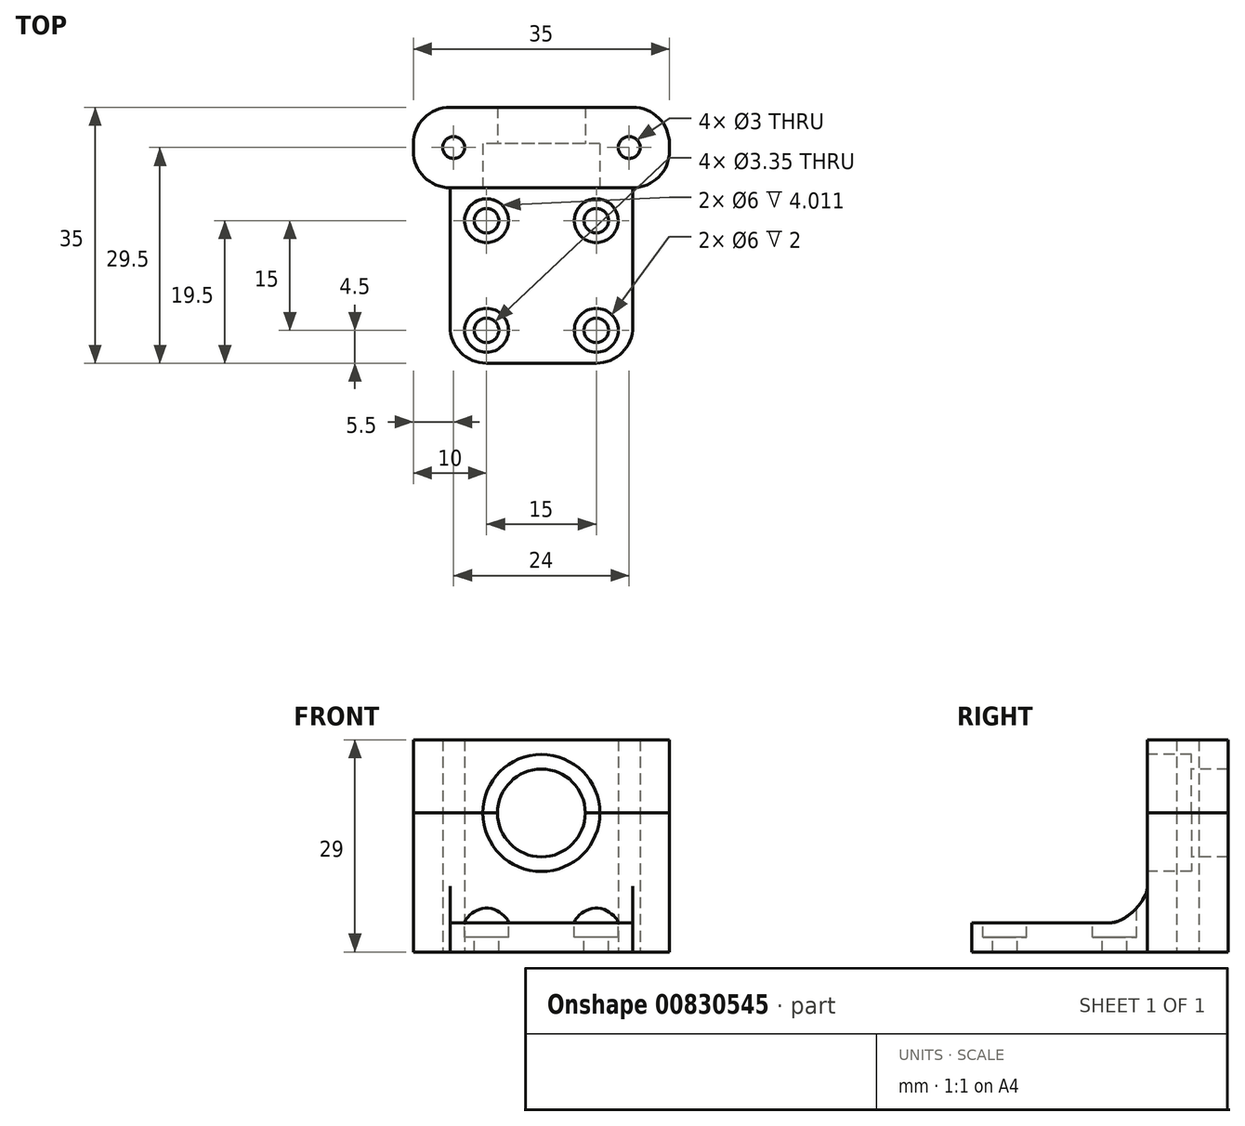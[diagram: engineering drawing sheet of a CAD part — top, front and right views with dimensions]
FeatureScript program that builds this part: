
annotation { "Feature Type Name" : "Feature", "Feature Type Description" : "" }
export const myFeature = defineFeature(function(context is Context, id is Id, definition is map)
    precondition{}
    {
        {
            var Q0;
            Q0=qCreatedBy(makeId("Right.planeOp"),FACE);
            var sketch = newSketch(context, id + "F0", { "sketchPlane" : qUnion([Q0])});
            skLineSegment(sketch, "E0", {"start": v(-12, -2) * mm, "end": v(23, -2) * mm});
            skLineSegment(sketch, "E1", {"start": v(23, -2) * mm, "end": v(23, 17) * mm});
            skLineSegment(sketch, "E2", {"start": v(23, 17) * mm, "end": v(12, 17) * mm});
            skLineSegment(sketch, "E3", {"start": v(12, 17) * mm, "end": v(12, 2) * mm});
            skLineSegment(sketch, "E4", {"start": v(12, 2) * mm, "end": v(-12, 2) * mm});
            skLineSegment(sketch, "E5", {"start": v(-12, 2) * mm, "end": v(-12, -2) * mm});
            skSolve(sketch);
        }
        {
            var Q0;
            Q0=qSketchRegion(id+"F0",true);
            extrude(context, id + "F1", {"entities" : qUnion([Q0]), "endBound" : BoundingType.SYMMETRIC, "depth" : 25 * mm, "offsetDistance" : 25 * mm});
        }
        {
            var Q0;
            Q0=makeQuery(id+"F1.opExtrude","SWEPT_FACE",FACE,{"disambiguationData":[OSD([sQuery(id+"F0.wireOp",EDGE,"E0")])]});
            var sketch = newSketch(context, id + "F2", { "sketchPlane" : qUnion([Q0])});
            skLineSegment(sketch, "E6.bottom", {"start": v(-17.5, -23) * mm, "end": v(17.5, -23) * mm});
            skLineSegment(sketch, "E6.top", {"start": v(-17.5, -12) * mm, "end": v(17.5, -12) * mm});
            skLineSegment(sketch, "E6.left", {"start": v(-17.5, -23) * mm, "end": v(-17.5, -12) * mm});
            skLineSegment(sketch, "E6.right", {"start": v(17.5, -23) * mm, "end": v(17.5, -12) * mm});
            skSolve(sketch);
        }
        {
            var Q0;
            Q0=qSketchRegion(id+"F2",true);
            var Q1;
            Q1=makeQuery(id+"F1.opExtrude","SWEPT_FACE",FACE,{"disambiguationData":[OSD([sQuery(id+"F0.wireOp",EDGE,"E2")])]});
            extrude(context, id + "F3", {"entities" : qUnion([Q0]), "operationType" : NewBodyOperationType.ADD, "endBound" : BoundingType.UP_TO_SURFACE, "oppositeDirection" : true, "depth" : 25 * mm, "endBoundEntityFace" : qUnion([Q1]), "offsetDistance" : 25 * mm});
        }
        {
            var Q0;
            Q0=makeQuery(id+"F1.opExtrude","SWEPT_FACE",FACE,{"disambiguationData":[OSD([sQuery(id+"F0.wireOp",EDGE,"E4")])]});
            var sketch = newSketch(context, id + "F4", { "sketchPlane" : qUnion([Q0])});
            skLineSegment(sketch, "E7.bottom", {"start": v(7.5, -7.5) * mm, "end": v(-7.5, -7.5) * mm, "construction": true});
            skLineSegment(sketch, "E7.top", {"start": v(7.5, 7.5) * mm, "end": v(-7.5, 7.5) * mm, "construction": true});
            skLineSegment(sketch, "E7.left", {"start": v(7.5, -7.5) * mm, "end": v(7.5, 7.5) * mm, "construction": true});
            skLineSegment(sketch, "E7.right", {"start": v(-7.5, -7.5) * mm, "end": v(-7.5, 7.5) * mm, "construction": true});
            skPoint(sketch, "E7.middle", {"position": v(0, 0) * mm});
            skCircle(sketch, "E8", {"center": v(7.5, 7.5) * mm, "radius": 3 * mm});
            skCircle(sketch, "E9", {"center": v(7.5, 7.5) * mm, "radius": 1.68 * mm});
            skCircle(sketch, "E10", {"center": v(7.5, -7.5) * mm, "radius": 3 * mm});
            skCircle(sketch, "E11", {"center": v(7.5, -7.5) * mm, "radius": 1.68 * mm});
            skCircle(sketch, "E12", {"center": v(-7.5, -7.5) * mm, "radius": 3 * mm});
            skCircle(sketch, "E13", {"center": v(-7.5, -7.5) * mm, "radius": 1.68 * mm});
            skCircle(sketch, "E14", {"center": v(-7.5, 7.5) * mm, "radius": 3 * mm});
            skCircle(sketch, "E15", {"center": v(-7.5, 7.5) * mm, "radius": 1.68 * mm});
            skSolve(sketch);
        }
        {
            var Q0;
            Q0=makeQuery(id+"F4.imprint","IMPRINT",FACE,{"disambiguationData":[TD([[makeQuery(id+"F4.imprint","IMPRINT",EDGE,{"derivedFrom":sQuery(id+"F4.wireOp",EDGE,"E9")}),1.0]])]});
            var Q1;
            Q1=makeQuery(id+"F4.imprint","IMPRINT",FACE,{"disambiguationData":[TD([[makeQuery(id+"F4.imprint","IMPRINT",EDGE,{"derivedFrom":sQuery(id+"F4.wireOp",EDGE,"E11")}),1.0]])]});
            var Q2;
            Q2=makeQuery(id+"F4.imprint","IMPRINT",FACE,{"disambiguationData":[TD([[makeQuery(id+"F4.imprint","IMPRINT",EDGE,{"derivedFrom":sQuery(id+"F4.wireOp",EDGE,"E13")}),1.0]])]});
            var Q3;
            Q3=makeQuery(id+"F4.imprint","IMPRINT",FACE,{"disambiguationData":[TD([[makeQuery(id+"F4.imprint","IMPRINT",EDGE,{"derivedFrom":sQuery(id+"F4.wireOp",EDGE,"E15")}),1.0]])]});
            extrude(context, id + "F5", {"entities" : qUnion([Q0, Q1, Q2, Q3]), "operationType" : NewBodyOperationType.REMOVE, "endBound" : BoundingType.THROUGH_ALL, "oppositeDirection" : true, "depth" : 25 * mm, "offsetDistance" : 25 * mm});
        }
        {
            var Q0;
            Q0=makeQuery(id+"F4.imprint","IMPRINT",FACE,{"disambiguationData":[TD([[makeQuery(id+"F4.imprint","IMPRINT",EDGE,{"derivedFrom":sQuery(id+"F4.wireOp",EDGE,"E14")}),1.0]])]});
            var Q1;
            Q1=makeQuery(id+"F4.imprint","IMPRINT",FACE,{"disambiguationData":[TD([[makeQuery(id+"F4.imprint","IMPRINT",EDGE,{"derivedFrom":sQuery(id+"F4.wireOp",EDGE,"E8")}),1.0]])]});
            var Q2;
            Q2=makeQuery(id+"F4.imprint","IMPRINT",FACE,{"disambiguationData":[TD([[makeQuery(id+"F4.imprint","IMPRINT",EDGE,{"derivedFrom":sQuery(id+"F4.wireOp",EDGE,"E10")}),1.0]])]});
            var Q3;
            Q3=makeQuery(id+"F4.imprint","IMPRINT",FACE,{"disambiguationData":[TD([[makeQuery(id+"F4.imprint","IMPRINT",EDGE,{"derivedFrom":sQuery(id+"F4.wireOp",EDGE,"E12")}),1.0]])]});
            extrude(context, id + "F6", {"entities" : qUnion([Q0, Q1, Q2, Q3]), "operationType" : NewBodyOperationType.REMOVE, "oppositeDirection" : true, "depth" : 2 * mm, "offsetDistance" : 25 * mm});
        }
        {
            var Q0;
            {var subQ0=sQuery(id+"F0.wireOp",EDGE,"E2");Q0=makeQuery(id+"F3.boolean.opBoolean","MERGE",FACE,{"derivedFrom":[makeQuery(id+"F1.opExtrude","SWEPT_FACE",FACE,{"disambiguationData":[OSD([subQ0])]}),makeQuery(id+"F3.opExtrude","CAP_FACE",FACE,{"disambiguationData":[OSD([subQ0])],"isStart":false})]});}
            extrude(context, id + "F7", {"entities" : qUnion([Q0]), "depth" : 10 * mm, "offsetDistance" : 25 * mm});
        }
        {
            var Q0;
            Q0=makeQuery(id+"F3.boolean.opBoolean","MERGE",FACE,{"derivedFrom":[makeQuery(id+"F1.opExtrude","SWEPT_FACE",FACE,{"disambiguationData":[OSD([sQuery(id+"F0.wireOp",EDGE,"E0")])]}),makeQuery(id+"F3.opExtrude","CAP_FACE",FACE,{"disambiguationData":[OSD([sQuery(id+"F2.wireOp",EDGE,"E6.bottom"),sQuery(id+"F2.wireOp",EDGE,"E6.top"),sQuery(id+"F2.wireOp",EDGE,"E6.left"),sQuery(id+"F2.wireOp",EDGE,"E6.right")])],"isStart":true})]});
            var sketch = newSketch(context, id + "F8", { "sketchPlane" : qUnion([Q0])});
            skLineSegment(sketch, "E16", {"start": v(-17.5, -17.5) * mm, "end": v(17.5, -17.5) * mm, "construction": true});
            skCircle(sketch, "E17", {"center": v(-12, -17.5) * mm, "radius": 1.5 * mm});
            skCircle(sketch, "E18", {"center": v(12, -17.5) * mm, "radius": 1.5 * mm});
            skSolve(sketch);
        }
        {
            var Q0;
            Q0=qSketchRegion(id+"F8",true);
            extrude(context, id + "F9", {"entities" : qUnion([Q0]), "operationType" : NewBodyOperationType.REMOVE, "endBound" : BoundingType.THROUGH_ALL, "oppositeDirection" : true, "depth" : 25 * mm, "offsetDistance" : 25 * mm});
        }
        {
            var Q0;
            Q0=makeQuery(id+"F3.boolean.opBoolean","MERGE",FACE,{"derivedFrom":[makeQuery(id+"F1.opExtrude","SWEPT_FACE",FACE,{"disambiguationData":[OSD([sQuery(id+"F0.wireOp",EDGE,"E3")])]}),makeQuery(id+"F3.opExtrude","SWEPT_FACE",FACE,{"disambiguationData":[OSD([sQuery(id+"F2.wireOp",EDGE,"E6.top")])]})]});
            var sketch = newSketch(context, id + "F10", { "sketchPlane" : qUnion([Q0])});
            skCircle(sketch, "E19", {"center": v(0, 17) * mm, "radius": 8 * mm});
            skCircle(sketch, "E20", {"center": v(0, 17) * mm, "radius": 6 * mm});
            skSolve(sketch);
        }
        {
            var Q0;
            {var subQ0=sQuery(id+"F10.wireOp",EDGE,"E20");var subQ1=sQuery(id+"F2.wireOp",EDGE,"E6.top");var subQ2=sQuery(id+"F0.wireOp",EDGE,"E0");var subQ4=makeQuery(id+"F2.imprint","INTERSECT",VERTEX,{"derivedFrom":[makeQuery(id+"F1.opExtrude","CAP_EDGE",EDGE,{"disambiguationData":[OSD([subQ2])],"isStart":true}),subQ1]});var subQ5=sQuery(id+"F0.wireOp",EDGE,"E2");var subQ6=makeQuery(id+"F3.boolean.opBoolean","MERGE",EDGE,{"derivedFrom":[makeQuery(id+"F1.opExtrude","SWEPT_EDGE",EDGE,{"disambiguationData":[OSD([subQ5,sQuery(id+"F0.wireOp",EDGE,"E3")])]}),makeQuery(id+"F3.opExtrude","TWEAK_EDGE",EDGE,{"derivedFrom":[makeQuery(id+"F1.opExtrude","SWEPT_FACE",FACE,{"disambiguationData":[OSD([subQ5])]}),makeQuery(id+"F2.imprint","IMPRINT",EDGE,{"disambiguationData":[TD([[makeQuery(id+"F2.imprint","INTERSECT",VERTEX,{"derivedFrom":[subQ1,sQuery(id+"F2.wireOp",EDGE,"E6.left")]}),-1.0]])],"derivedFrom":subQ1}),makeQuery(id+"F2.imprint","IMPRINT",EDGE,{"disambiguationData":[TD([[subQ4,-1.0]])],"derivedFrom":subQ1}),makeQuery(id+"F2.imprint","IMPRINT",EDGE,{"disambiguationData":[TD([[makeQuery(id+"F2.imprint","INTERSECT",VERTEX,{"derivedFrom":[subQ1,sQuery(id+"F2.wireOp",EDGE,"E6.right")]}),1.0]])],"derivedFrom":subQ1})]})]});var subQ7=makeQuery(id+"F10.imprint","INTERSECT",VERTEX,{"disambiguationData":[OD(0.0)],"derivedFrom":[subQ6,subQ0]});Q0=makeQuery(id+"F10.imprint","IMPRINT",FACE,{"disambiguationData":[TD([[makeQuery(id+"F10.imprint","IMPRINT",EDGE,{"disambiguationData":[TD([[subQ7,-1.0]])],"derivedFrom":subQ0}),1.0]])]});}
            var Q1;
            {var subQ0=sQuery(id+"F10.wireOp",EDGE,"E20");var subQ1=sQuery(id+"F2.wireOp",EDGE,"E6.top");var subQ2=sQuery(id+"F0.wireOp",EDGE,"E0");var subQ4=makeQuery(id+"F2.imprint","INTERSECT",VERTEX,{"derivedFrom":[makeQuery(id+"F1.opExtrude","CAP_EDGE",EDGE,{"disambiguationData":[OSD([subQ2])],"isStart":true}),subQ1]});var subQ5=sQuery(id+"F0.wireOp",EDGE,"E2");var subQ6=makeQuery(id+"F3.boolean.opBoolean","MERGE",EDGE,{"derivedFrom":[makeQuery(id+"F1.opExtrude","SWEPT_EDGE",EDGE,{"disambiguationData":[OSD([subQ5,sQuery(id+"F0.wireOp",EDGE,"E3")])]}),makeQuery(id+"F3.opExtrude","TWEAK_EDGE",EDGE,{"derivedFrom":[makeQuery(id+"F1.opExtrude","SWEPT_FACE",FACE,{"disambiguationData":[OSD([subQ5])]}),makeQuery(id+"F2.imprint","IMPRINT",EDGE,{"disambiguationData":[TD([[makeQuery(id+"F2.imprint","INTERSECT",VERTEX,{"derivedFrom":[subQ1,sQuery(id+"F2.wireOp",EDGE,"E6.left")]}),-1.0]])],"derivedFrom":subQ1}),makeQuery(id+"F2.imprint","IMPRINT",EDGE,{"disambiguationData":[TD([[subQ4,-1.0]])],"derivedFrom":subQ1}),makeQuery(id+"F2.imprint","IMPRINT",EDGE,{"disambiguationData":[TD([[makeQuery(id+"F2.imprint","INTERSECT",VERTEX,{"derivedFrom":[subQ1,sQuery(id+"F2.wireOp",EDGE,"E6.right")]}),1.0]])],"derivedFrom":subQ1})]})]});var subQ7=makeQuery(id+"F10.imprint","INTERSECT",VERTEX,{"disambiguationData":[OD(0.0)],"derivedFrom":[subQ6,subQ0]});Q1=makeQuery(id+"F10.imprint","IMPRINT",FACE,{"disambiguationData":[TD([[makeQuery(id+"F10.imprint","IMPRINT",EDGE,{"disambiguationData":[TD([[subQ7,1.0]])],"derivedFrom":subQ0}),1.0]])]});}
            var Q2;
            Q2=sQuery(id+"F10.wireOp",EDGE,"E20");
            extrude(context, id + "F11", {"entities" : qUnion([Q0, Q1]), "operationType" : NewBodyOperationType.REMOVE, "surfaceEntities" : qUnion([Q2]), "endBound" : BoundingType.THROUGH_ALL, "oppositeDirection" : true, "depth" : 25 * mm, "offsetDistance" : 25 * mm});
        }
        {
            var Q0;
            {var subQ0=sQuery(id+"F10.wireOp",EDGE,"E19");var subQ1=sQuery(id+"F2.wireOp",EDGE,"E6.top");var subQ2=sQuery(id+"F0.wireOp",EDGE,"E0");var subQ4=makeQuery(id+"F2.imprint","INTERSECT",VERTEX,{"derivedFrom":[makeQuery(id+"F1.opExtrude","CAP_EDGE",EDGE,{"disambiguationData":[OSD([subQ2])],"isStart":true}),subQ1]});var subQ5=sQuery(id+"F0.wireOp",EDGE,"E2");var subQ6=makeQuery(id+"F3.boolean.opBoolean","MERGE",EDGE,{"derivedFrom":[makeQuery(id+"F1.opExtrude","SWEPT_EDGE",EDGE,{"disambiguationData":[OSD([subQ5,sQuery(id+"F0.wireOp",EDGE,"E3")])]}),makeQuery(id+"F3.opExtrude","TWEAK_EDGE",EDGE,{"derivedFrom":[makeQuery(id+"F1.opExtrude","SWEPT_FACE",FACE,{"disambiguationData":[OSD([subQ5])]}),makeQuery(id+"F2.imprint","IMPRINT",EDGE,{"disambiguationData":[TD([[makeQuery(id+"F2.imprint","INTERSECT",VERTEX,{"derivedFrom":[subQ1,sQuery(id+"F2.wireOp",EDGE,"E6.left")]}),-1.0]])],"derivedFrom":subQ1}),makeQuery(id+"F2.imprint","IMPRINT",EDGE,{"disambiguationData":[TD([[subQ4,-1.0]])],"derivedFrom":subQ1}),makeQuery(id+"F2.imprint","IMPRINT",EDGE,{"disambiguationData":[TD([[makeQuery(id+"F2.imprint","INTERSECT",VERTEX,{"derivedFrom":[subQ1,sQuery(id+"F2.wireOp",EDGE,"E6.right")]}),1.0]])],"derivedFrom":subQ1})]})]});var subQ7=makeQuery(id+"F10.imprint","INTERSECT",VERTEX,{"disambiguationData":[OD(0.0)],"derivedFrom":[subQ6,subQ0]});Q0=makeQuery(id+"F10.imprint","IMPRINT",FACE,{"disambiguationData":[TD([[makeQuery(id+"F10.imprint","IMPRINT",EDGE,{"disambiguationData":[TD([[subQ7,1.0]])],"derivedFrom":subQ0}),1.0]])]});}
            var Q1;
            {var subQ0=sQuery(id+"F10.wireOp",EDGE,"E19");var subQ1=sQuery(id+"F2.wireOp",EDGE,"E6.top");var subQ2=sQuery(id+"F0.wireOp",EDGE,"E0");var subQ4=makeQuery(id+"F2.imprint","INTERSECT",VERTEX,{"derivedFrom":[makeQuery(id+"F1.opExtrude","CAP_EDGE",EDGE,{"disambiguationData":[OSD([subQ2])],"isStart":true}),subQ1]});var subQ5=sQuery(id+"F0.wireOp",EDGE,"E2");var subQ6=makeQuery(id+"F3.boolean.opBoolean","MERGE",EDGE,{"derivedFrom":[makeQuery(id+"F1.opExtrude","SWEPT_EDGE",EDGE,{"disambiguationData":[OSD([subQ5,sQuery(id+"F0.wireOp",EDGE,"E3")])]}),makeQuery(id+"F3.opExtrude","TWEAK_EDGE",EDGE,{"derivedFrom":[makeQuery(id+"F1.opExtrude","SWEPT_FACE",FACE,{"disambiguationData":[OSD([subQ5])]}),makeQuery(id+"F2.imprint","IMPRINT",EDGE,{"disambiguationData":[TD([[makeQuery(id+"F2.imprint","INTERSECT",VERTEX,{"derivedFrom":[subQ1,sQuery(id+"F2.wireOp",EDGE,"E6.left")]}),-1.0]])],"derivedFrom":subQ1}),makeQuery(id+"F2.imprint","IMPRINT",EDGE,{"disambiguationData":[TD([[subQ4,-1.0]])],"derivedFrom":subQ1}),makeQuery(id+"F2.imprint","IMPRINT",EDGE,{"disambiguationData":[TD([[makeQuery(id+"F2.imprint","INTERSECT",VERTEX,{"derivedFrom":[subQ1,sQuery(id+"F2.wireOp",EDGE,"E6.right")]}),1.0]])],"derivedFrom":subQ1})]})]});var subQ7=makeQuery(id+"F10.imprint","INTERSECT",VERTEX,{"disambiguationData":[OD(0.0)],"derivedFrom":[subQ6,subQ0]});Q1=makeQuery(id+"F10.imprint","IMPRINT",FACE,{"disambiguationData":[TD([[makeQuery(id+"F10.imprint","IMPRINT",EDGE,{"disambiguationData":[TD([[subQ7,-1.0]])],"derivedFrom":subQ0}),1.0]])]});}
            extrude(context, id + "F12", {"entities" : qUnion([Q0, Q1]), "operationType" : NewBodyOperationType.REMOVE, "oppositeDirection" : true, "depth" : 6 * mm, "offsetDistance" : 25 * mm});
        }
        {
            var Q0;
            Q0=makeQuery(id+"F3.opExtrude","SWEPT_EDGE",EDGE,{"disambiguationData":[OSD([sQuery(id+"F2.wireOp",EDGE,"E6.top"),sQuery(id+"F2.wireOp",EDGE,"E6.left")])]});
            var Q1;
            Q1=makeQuery(id+"F7.opExtrude","SWEPT_EDGE",EDGE,{"disambiguationData":[OSD([sQuery(id+"F0.wireOp",EDGE,"E2"),sQuery(id+"F2.wireOp",EDGE,"E6.top"),sQuery(id+"F2.wireOp",EDGE,"E6.left")])]});
            var Q2;
            Q2=makeQuery(id+"F7.opExtrude","SWEPT_EDGE",EDGE,{"disambiguationData":[OSD([sQuery(id+"F0.wireOp",EDGE,"E2"),sQuery(id+"F2.wireOp",EDGE,"E6.bottom"),sQuery(id+"F2.wireOp",EDGE,"E6.left")])]});
            var Q3;
            Q3=makeQuery(id+"F3.opExtrude","SWEPT_EDGE",EDGE,{"disambiguationData":[OSD([sQuery(id+"F2.wireOp",EDGE,"E6.bottom"),sQuery(id+"F2.wireOp",EDGE,"E6.left")])]});
            var Q4;
            Q4=makeQuery(id+"F3.opExtrude","SWEPT_EDGE",EDGE,{"disambiguationData":[OSD([sQuery(id+"F2.wireOp",EDGE,"E6.top"),sQuery(id+"F2.wireOp",EDGE,"E6.right")])]});
            var Q5;
            Q5=makeQuery(id+"F7.opExtrude","SWEPT_EDGE",EDGE,{"disambiguationData":[OSD([sQuery(id+"F0.wireOp",EDGE,"E2"),sQuery(id+"F2.wireOp",EDGE,"E6.top"),sQuery(id+"F2.wireOp",EDGE,"E6.right")])]});
            var Q6;
            Q6=makeQuery(id+"F7.opExtrude","SWEPT_EDGE",EDGE,{"disambiguationData":[OSD([sQuery(id+"F0.wireOp",EDGE,"E2"),sQuery(id+"F2.wireOp",EDGE,"E6.bottom"),sQuery(id+"F2.wireOp",EDGE,"E6.right")])]});
            var Q7;
            Q7=makeQuery(id+"F3.opExtrude","SWEPT_EDGE",EDGE,{"disambiguationData":[OSD([sQuery(id+"F2.wireOp",EDGE,"E6.bottom"),sQuery(id+"F2.wireOp",EDGE,"E6.right")])]});
            var Q8;
            Q8=makeQuery(id+"F1.opExtrude","CAP_EDGE",EDGE,{"disambiguationData":[OSD([sQuery(id+"F0.wireOp",EDGE,"E5")])],"isStart":false});
            var Q9;
            Q9=makeQuery(id+"F1.opExtrude","CAP_EDGE",EDGE,{"disambiguationData":[OSD([sQuery(id+"F0.wireOp",EDGE,"E5")])],"isStart":true});
            fillet(context, id + "F13", {"entities" : qUnion([Q0, Q1, Q2, Q3, Q4, Q5, Q6, Q7, Q8, Q9]), "radius" : 5 * mm, "tangentPropagation" : true, "allowEdgeOverflow" : false});
        }
        {
            var Q0;
            Q0=makeQuery(id+"F1.opExtrude","SWEPT_EDGE",EDGE,{"disambiguationData":[OSD([sQuery(id+"F0.wireOp",EDGE,"E3"),sQuery(id+"F0.wireOp",EDGE,"E4")])]});
            fillet(context, id + "F14", {"entities" : qUnion([Q0]), "radius" : 5 * mm, "tangentPropagation" : true, "rho" : .3, "crossSection" : FilletCrossSection.CONIC, "allowEdgeOverflow" : false});
        }
    });
